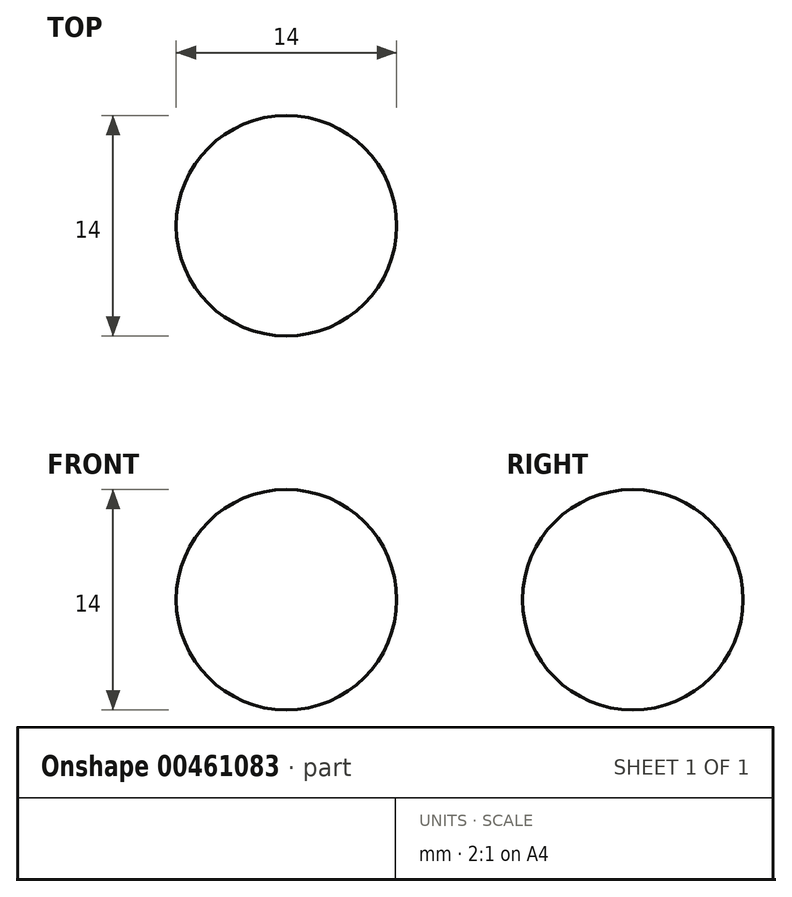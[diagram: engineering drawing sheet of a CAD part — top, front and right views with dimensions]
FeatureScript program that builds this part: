
annotation { "Feature Type Name" : "Feature", "Feature Type Description" : "" }
export const myFeature = defineFeature(function(context is Context, id is Id, definition is map)
    precondition{}
    {
        {
            var Q0;
            Q0=qCreatedBy(makeId("Front.planeOp"),FACE);
            var sketch = newSketch(context, id + "F0", { "sketchPlane" : qUnion([Q0])});
            skLineSegment(sketch, "E0", {"start": v(0, 0) * mm, "end": v(0, 14) * mm});
            skArc(sketch, "E1", {"start": v(0, 14) * mm, "mid": v(-7, 7) * mm, "end": v(0, 0) * mm});
            skSolve(sketch);
        }
        {
            var Q0;
            Q0=makeQuery(id+"F0.imprint","IMPRINT",FACE,{"disambiguationData":[TD([[makeQuery(id+"F0.imprint","IMPRINT",EDGE,{"derivedFrom":sQuery(id+"F0.wireOp",EDGE,"E0")}),1.0]])]});
            var Q1;
            Q1=sQuery(id+"F0.wireOp",EDGE,"E0");
            revolve(context, id + "F1", {"entities" : qUnion([Q0]), "axis" : qUnion([Q1]), "revolveType" : RevolveType.FULL});
        }
    });
